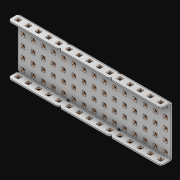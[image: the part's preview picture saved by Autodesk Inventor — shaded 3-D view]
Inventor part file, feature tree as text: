
AUTODESK INVENTOR PART (.ipt)
format: ipt  version: 2021 (Build 250183000, 183)  size: 3,203,072 bytes
history: native  units: in
note: dims shown in document units (in); Inventor stores cm internally (conversion verified against a paired STEP export)
features: extrude x106, other x105, sketch x4, thicken_offset x3, pattern_linear x3, imported_body x1
ambient origin geometry x8: Origin, YZ Plane, XZ Plane, XY Plane, X Axis, Y Axis, Z Axis, Center Point
bodies: Solid1 (feature_tree)
feature tree (222):
  thicken_offset  "Thicken1"
  thicken_offset  "Thicken2"
  thicken_offset  "Thicken3"
  pattern_linear  "Rectangular Pattern1"  Spacing1=0.001in  [1 undecoded]
  pattern_linear  "Rectangular Pattern2"  Spacing1=0.001in  [1 undecoded]
  pattern_linear  "Rectangular Pattern3"  Spacing1=0.182in  [1 undecoded]
  extrude  "Extrusion1"  Depth=0.063in TaperAngle=0.0deg
  sketch  "Sketch1"  dims[d0=0.001in]
  other  "Srf1"
  sketch  "Sketch2"  dims[d1=0.001in]
  other  "Srf2"
  sketch  "Sketch3"  dims[d2=0.001in]
  other  "Srf3"
  other  "Srf4"
  other  "Srf5"
  other  "Srf6"
  other  "Srf7"
  other  "Srf8"
  other  "Srf9"
  other  "Srf10"
  other  "Srf11"
  other  "Srf12"
  other  "Srf13"
  other  "Srf14"
  other  "Srf15"
  other  "Srf16"
  other  "Srf17"
  other  "Srf38"
  other  "Srf39"
  other  "Srf40"
  other  "Srf41"
  other  "Srf42"
  other  "Srf43"
  other  "Srf44"
  other  "Srf45"
  other  "Srf46"
  other  "Srf47"
  other  "Srf48"
  other  "Srf49"
  other  "Srf50"
  other  "Srf51"
  other  "Srf72"
  other  "Srf73"
  other  "Srf74"
  other  "Srf75"
  other  "Srf76"
  other  "Srf77"
  other  "Srf78"
  other  "Srf79"
  other  "Srf80"
  other  "Srf81"
  other  "Srf82"
  other  "Srf83"
  other  "Srf84"
  other  "Srf85"
  other  "Srf106"
  other  "Srf107"
  other  "Srf108"
  other  "Srf109"
  other  "Srf110"
  other  "Srf111"
  other  "Srf112"
  other  "Srf113"
  other  "Srf114"
  other  "Srf115"
  other  "Srf116"
  other  "Srf117"
  other  "Srf118"
  other  "Srf119"
  other  "Srf120"
  other  "Srf141"
  other  "Srf142"
  other  "Srf143"
  other  "Srf144"
  other  "Srf145"
  other  "Srf146"
  other  "Srf147"
  other  "Srf148"
  other  "Srf149"
  other  "Srf150"
  other  "Srf151"
  other  "Srf152"
  other  "Srf153"
  other  "Srf154"
  other  "Srf155"
  other  "Srf176"
  other  "Srf177"
  other  "Srf178"
  other  "Srf179"
  other  "Srf180"
  other  "Srf181"
  other  "Srf182"
  other  "Srf183"
  other  "Srf184"
  other  "Srf185"
  other  "Srf186"
  other  "Srf187"
  other  "Srf188"
  other  "Srf189"
  other  "Srf190"
  other  "Srf211"
  other  "Srf212"
  other  "Srf213"
  other  "Srf214"
  other  "Srf215"
  other  "Srf216"
  other  "Srf217"
  other  "Srf218"
  other  "Srf219"
  other  "Srf220"
  other  "Srf221"
  other  "Srf222"
  other  "Srf223"
  other  "Srf224"
  other  "Srf225"
  sketch  "Sketch4"  dims[d3=0.001in d4=0.001in d5=0.001in d6=0.182in d7=0.063in d8=0.0in d9=0.182in d10=0.063in d11=0.0in d12=0.182in d13=0.063in d14=0.0in d17=0.5in d18=5.9055in d20=0.5in d21=5.9055in d23=0.5in d24=1.9685in d26=0.5in d27=10.0in d28=0.0in]
  imported_body  "Imported1"
  extrude  "ExtrusionSrf1"  Depth=0.063in
  extrude  "ExtrusionSrf2"  Depth=0.063in TaperAngle=0.0deg
  extrude  "ExtrusionSrf3"  Depth=0.063in
  extrude  "ExtrusionSrf4"  Depth=0.063in TaperAngle=0.0deg
  extrude  "ExtrusionSrf5"  Depth=0.063in
  extrude  "ExtrusionSrf6"  Depth=0.063in
  extrude  "ExtrusionSrf7"  Depth=0.063in
  extrude  "ExtrusionSrf8"  Depth=0.063in
  extrude  "ExtrusionSrf9"  Depth=0.063in
  extrude  "ExtrusionSrf10"  Depth=0.063in
  extrude  "ExtrusionSrf11"  Depth=0.063in
  extrude  "ExtrusionSrf12"  TaperAngle=0.0deg  [1 undecoded]
  extrude  "ExtrusionSrf13"  [1 undecoded]
  extrude  "ExtrusionSrf14"  [1 undecoded]
  extrude  "ExtrusionSrf15"  [1 undecoded]
  extrude  "ExtrusionSrf16"  [1 undecoded]
  extrude  "ExtrusionSrf17"  [1 undecoded]
  extrude  "ExtrusionSrf38"  [1 undecoded]
  extrude  "ExtrusionSrf39"  [1 undecoded]
  extrude  "ExtrusionSrf40"  [1 undecoded]
  extrude  "ExtrusionSrf41"  [1 undecoded]
  extrude  "ExtrusionSrf42"  [1 undecoded]
  extrude  "ExtrusionSrf43"  [1 undecoded]
  extrude  "ExtrusionSrf44"  [1 undecoded]
  extrude  "ExtrusionSrf45"  [1 undecoded]
  extrude  "ExtrusionSrf46"  [1 undecoded]
  extrude  "ExtrusionSrf47"  [1 undecoded]
  extrude  "ExtrusionSrf48"  [1 undecoded]
  extrude  "ExtrusionSrf49"  [1 undecoded]
  extrude  "ExtrusionSrf50"  [1 undecoded]
  extrude  "ExtrusionSrf51"  [1 undecoded]
  extrude  "ExtrusionSrf72"  [1 undecoded]
  extrude  "ExtrusionSrf73"  [1 undecoded]
  extrude  "ExtrusionSrf74"  [1 undecoded]
  extrude  "ExtrusionSrf75"  [1 undecoded]
  extrude  "ExtrusionSrf76"  [1 undecoded]
  extrude  "ExtrusionSrf77"  [1 undecoded]
  extrude  "ExtrusionSrf78"  [1 undecoded]
  extrude  "ExtrusionSrf79"  [1 undecoded]
  extrude  "ExtrusionSrf80"  [1 undecoded]
  extrude  "ExtrusionSrf81"  [1 undecoded]
  extrude  "ExtrusionSrf82"  [1 undecoded]
  extrude  "ExtrusionSrf83"  [1 undecoded]
  extrude  "ExtrusionSrf84"  [1 undecoded]
  extrude  "ExtrusionSrf85"  [1 undecoded]
  extrude  "ExtrusionSrf106"  [1 undecoded]
  extrude  "ExtrusionSrf107"  [1 undecoded]
  extrude  "ExtrusionSrf108"  [1 undecoded]
  extrude  "ExtrusionSrf109"  [1 undecoded]
  extrude  "ExtrusionSrf110"  [1 undecoded]
  extrude  "ExtrusionSrf111"  [1 undecoded]
  extrude  "ExtrusionSrf112"  [1 undecoded]
  extrude  "ExtrusionSrf113"  [1 undecoded]
  extrude  "ExtrusionSrf114"  [1 undecoded]
  extrude  "ExtrusionSrf115"  [1 undecoded]
  extrude  "ExtrusionSrf116"  [1 undecoded]
  extrude  "ExtrusionSrf117"  [1 undecoded]
  extrude  "ExtrusionSrf118"  [1 undecoded]
  extrude  "ExtrusionSrf119"  [1 undecoded]
  extrude  "ExtrusionSrf120"  [1 undecoded]
  extrude  "ExtrusionSrf141"  [1 undecoded]
  extrude  "ExtrusionSrf142"  [1 undecoded]
  extrude  "ExtrusionSrf143"  [1 undecoded]
  extrude  "ExtrusionSrf144"  [1 undecoded]
  extrude  "ExtrusionSrf145"  [1 undecoded]
  extrude  "ExtrusionSrf146"  [1 undecoded]
  extrude  "ExtrusionSrf147"  [1 undecoded]
  extrude  "ExtrusionSrf148"  [1 undecoded]
  extrude  "ExtrusionSrf149"  [1 undecoded]
  extrude  "ExtrusionSrf150"  [1 undecoded]
  extrude  "ExtrusionSrf151"  [1 undecoded]
  extrude  "ExtrusionSrf152"  [1 undecoded]
  extrude  "ExtrusionSrf153"  [1 undecoded]
  extrude  "ExtrusionSrf154"  [1 undecoded]
  extrude  "ExtrusionSrf155"  [1 undecoded]
  extrude  "ExtrusionSrf176"  [1 undecoded]
  extrude  "ExtrusionSrf177"  [1 undecoded]
  extrude  "ExtrusionSrf178"  [1 undecoded]
  extrude  "ExtrusionSrf179"  [1 undecoded]
  extrude  "ExtrusionSrf180"  [1 undecoded]
  extrude  "ExtrusionSrf181"  [1 undecoded]
  extrude  "ExtrusionSrf182"  [1 undecoded]
  extrude  "ExtrusionSrf183"  [1 undecoded]
  extrude  "ExtrusionSrf184"  [1 undecoded]
  extrude  "ExtrusionSrf185"  [1 undecoded]
  extrude  "ExtrusionSrf186"  [1 undecoded]
  extrude  "ExtrusionSrf187"  [1 undecoded]
  extrude  "ExtrusionSrf188"  [1 undecoded]
  extrude  "ExtrusionSrf189"  [1 undecoded]
  extrude  "ExtrusionSrf190"  [1 undecoded]
  extrude  "ExtrusionSrf211"  [1 undecoded]
  extrude  "ExtrusionSrf212"  [1 undecoded]
  extrude  "ExtrusionSrf213"  [1 undecoded]
  extrude  "ExtrusionSrf214"  [1 undecoded]
  extrude  "ExtrusionSrf215"  [1 undecoded]
  extrude  "ExtrusionSrf216"  [1 undecoded]
  extrude  "ExtrusionSrf217"  [1 undecoded]
  extrude  "ExtrusionSrf218"  [1 undecoded]
  extrude  "ExtrusionSrf219"  [1 undecoded]
  extrude  "ExtrusionSrf220"  [1 undecoded]
  extrude  "ExtrusionSrf221"  [1 undecoded]
  extrude  "ExtrusionSrf222"  [1 undecoded]
  extrude  "ExtrusionSrf223"  [1 undecoded]
  extrude  "ExtrusionSrf224"  [1 undecoded]
  extrude  "ExtrusionSrf225"  [1 undecoded]
note: 97 required parameter values undecoded (feature->parameter linkage not recoverable at this tier; creation-order binding heuristic only, values carry confidence <= 0.55)
